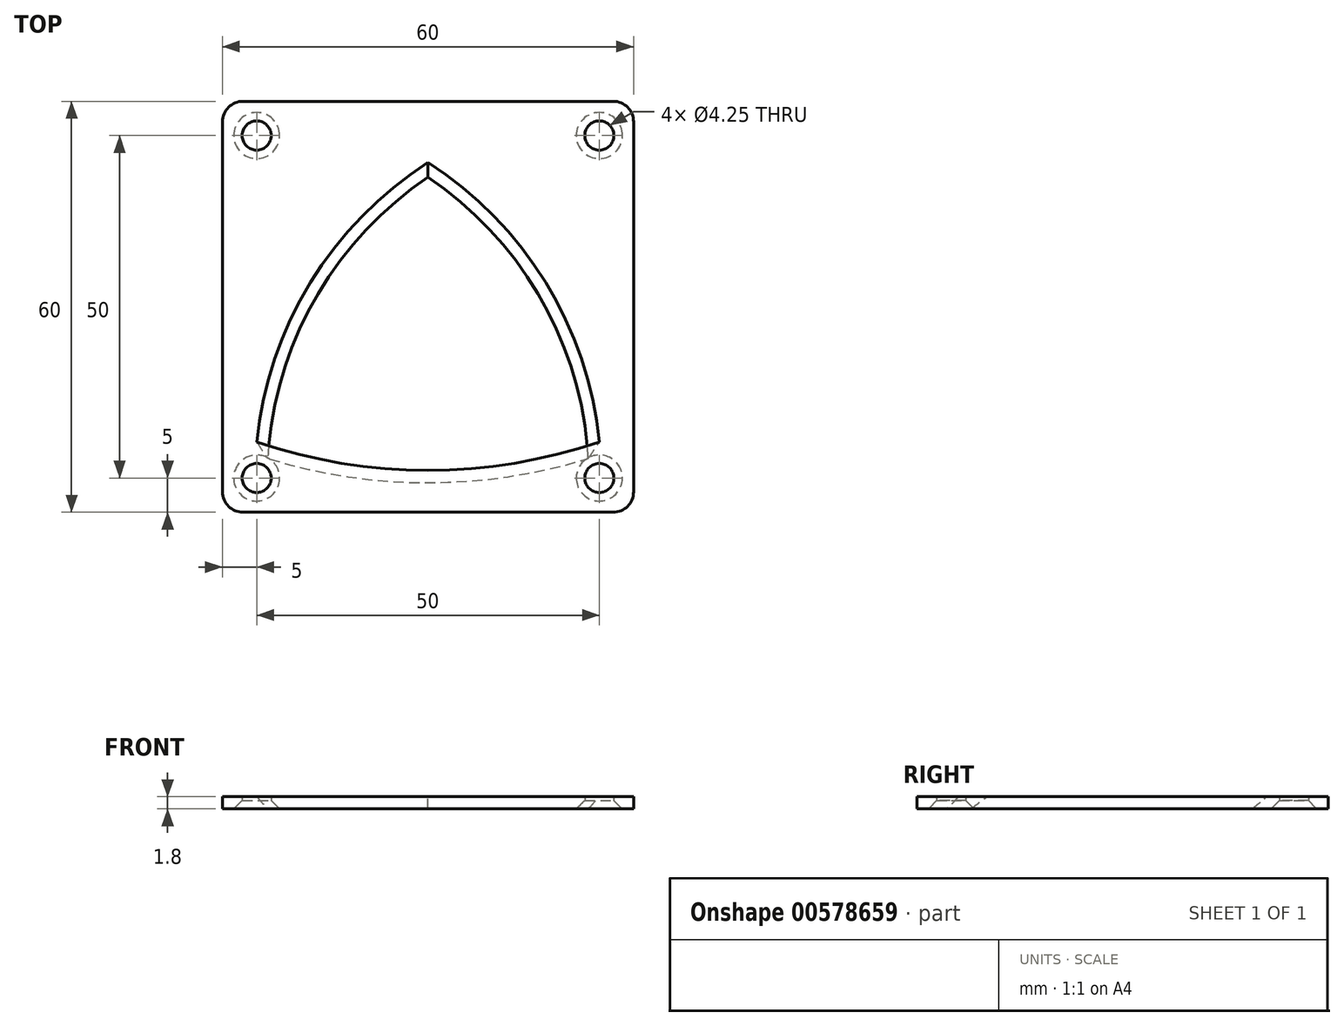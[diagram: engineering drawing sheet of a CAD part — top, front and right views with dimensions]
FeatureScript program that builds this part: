
annotation { "Feature Type Name" : "Feature", "Feature Type Description" : "" }
export const myFeature = defineFeature(function(context is Context, id is Id, definition is map)
    precondition{}
    {
        {
            var Q0;
            Q0=qCreatedBy(makeId("Top.planeOp"),FACE);
            var sketch = newSketch(context, id + "F0", { "sketchPlane" : qUnion([Q0])});
            skLineSegment(sketch, "E0.bottom", {"start": v(25, -25) * mm, "end": v(-25, -25) * mm});
            skLineSegment(sketch, "E0.top", {"start": v(25, 25) * mm, "end": v(-25, 25) * mm});
            skLineSegment(sketch, "E0.left", {"start": v(25, -25) * mm, "end": v(25, 25) * mm});
            skLineSegment(sketch, "E0.right", {"start": v(-25, -25) * mm, "end": v(-25, 25) * mm});
            skPoint(sketch, "E0.middle", {"position": v(0, 0) * mm});
            skLineSegment(sketch, "E1.bottom", {"start": v(30, -30) * mm, "end": v(-30, -30) * mm});
            skLineSegment(sketch, "E1.top", {"start": v(30, 30) * mm, "end": v(-30, 30) * mm});
            skLineSegment(sketch, "E1.left", {"start": v(30, -30) * mm, "end": v(30, 30) * mm});
            skLineSegment(sketch, "E1.right", {"start": v(-30, -30) * mm, "end": v(-30, 30) * mm});
            skLineSegment(sketch, "E2.bottom", {"start": v(-30, -30) * mm, "end": v(30, -30) * mm});
            skLineSegment(sketch, "E2.top", {"start": v(-30, -50) * mm, "end": v(30, -50) * mm});
            skLineSegment(sketch, "E2.left", {"start": v(-30, -30) * mm, "end": v(-30, -50) * mm});
            skLineSegment(sketch, "E2.right", {"start": v(30, -30) * mm, "end": v(30, -50) * mm});
            skPoint(sketch, "E3", {"position": v(-12.75, -33.65) * mm});
            skPoint(sketch, "E4", {"position": v(12.75, -33.65) * mm});
            skPoint(sketch, "E5", {"position": v(0, -33.65) * mm});
            skPoint(sketch, "E5.positionSnap0", {"position": v(0, -30) * mm});
            skLineSegment(sketch, "E6", {"start": v(-20, -20) * mm, "end": v(20, -20) * mm});
            skLineSegment(sketch, "E7", {"start": v(20, -20) * mm, "end": v(0, 15) * mm});
            skLineSegment(sketch, "E8", {"start": v(0, 15) * mm, "end": v(-20, -20) * mm});
            skPoint(sketch, "E9", {"position": v(0, -20) * mm});
            skArc(sketch, "E10", {"start": v(-20, -20) * mm, "mid": v(0, -22.68) * mm, "end": v(20, -20) * mm});
            skArc(sketch, "E11", {"start": v(0, 15) * mm, "mid": v(-13.68, -0.4) * mm, "end": v(-20, -20) * mm});
            skArc(sketch, "E12", {"start": v(20, -20) * mm, "mid": v(13.68, -0.4) * mm, "end": v(0, 15) * mm});
            skSolve(sketch);
        }
        {
            var Q0;
            Q0=makeQuery(id+"F0.imprint","IMPRINT",FACE,{"disambiguationData":[TD([[makeQuery(id+"F0.imprint","IMPRINT",EDGE,{"derivedFrom":sQuery(id+"F0.wireOp",EDGE,"E2.bottom")}),-1.0]])]});
            var Q1;
            Q1=makeQuery(id+"F0.imprint","IMPRINT",FACE,{"disambiguationData":[TD([[makeQuery(id+"F0.imprint","IMPRINT",EDGE,{"derivedFrom":sQuery(id+"F0.wireOp",EDGE,"E0.bottom")}),1.0]])]});
            var Q2;
            Q2=makeQuery(id+"F0.imprint","IMPRINT",FACE,{"disambiguationData":[TD([[makeQuery(id+"F0.imprint","IMPRINT",EDGE,{"derivedFrom":sQuery(id+"F0.wireOp",EDGE,"E0.bottom")}),-1.0]])]});
            extrude(context, id + "F1", {"entities" : qUnion([Q0, Q1, Q2]), "depth" : 1.8 * mm, "offsetDistance" : 25 * mm});
        }
        {
            var Q0;
            Q0=sQuery(id+"F0.wireOp",VERTEX,"E0.right.start");
            var Q1;
            Q1=sQuery(id+"F0.wireOp",VERTEX,"E0.left.start");
            var Q2;
            Q2=sQuery(id+"F0.wireOp",VERTEX,"E0.left.end");
            var Q3;
            Q3=sQuery(id+"F0.wireOp",VERTEX,"E0.right.end");
            var Q4;
            Q4=makeQuery(id+"F1.opExtrude","SWEPT_BODY",BODY,{"disambiguationData":[OSD([sQuery(id+"F0.wireOp",EDGE,"E1.top"),sQuery(id+"F0.wireOp",EDGE,"E1.left"),sQuery(id+"F0.wireOp",EDGE,"E1.right"),sQuery(id+"F0.wireOp",EDGE,"E2.top"),sQuery(id+"F0.wireOp",EDGE,"E2.left"),sQuery(id+"F0.wireOp",EDGE,"E2.right"),sQuery(id+"F0.wireOp",EDGE,"E10"),sQuery(id+"F0.wireOp",EDGE,"E11"),sQuery(id+"F0.wireOp",EDGE,"E12")])]});
            hole(context, id + "F2", {"style" : HoleStyle.C_SINK, "endStyle" : HoleEndStyle.BLIND, "oppositeDirection" : true, "holeDiameter" : 4.25 * mm, "cSinkDiameter" : 6.72 * mm, "cSinkAngle" : 90 * degree, "majorDiameter" : 5 * mm, "holeDepth" : 15 * mm, "isTappedThrough" : true, "tappedDepth" : 12 * mm, "tapClearance" : 3, "locations" : qUnion([Q0, Q1, Q2, Q3]), "scope" : qUnion([Q4])});
        }
        {
            var Q0;
            Q0=sQuery(id+"F0.wireOp",VERTEX,"E3");
            var Q1;
            Q1=sQuery(id+"F0.wireOp",VERTEX,"E4");
            var Q2;
            Q2=makeQuery(id+"F1.opExtrude","SWEPT_BODY",BODY,{"disambiguationData":[OSD([sQuery(id+"F0.wireOp",EDGE,"E1.top"),sQuery(id+"F0.wireOp",EDGE,"E1.left"),sQuery(id+"F0.wireOp",EDGE,"E1.right"),sQuery(id+"F0.wireOp",EDGE,"E2.top"),sQuery(id+"F0.wireOp",EDGE,"E2.left"),sQuery(id+"F0.wireOp",EDGE,"E2.right"),sQuery(id+"F0.wireOp",EDGE,"E10"),sQuery(id+"F0.wireOp",EDGE,"E11"),sQuery(id+"F0.wireOp",EDGE,"E12")])]});
            hole(context, id + "F3", {"style" : HoleStyle.C_BORE, "endStyle" : HoleEndStyle.BLIND, "oppositeDirection" : true, "holeDiameter" : 3 * mm, "cBoreDiameter" : 6.5 * mm, "cBoreDepth" : .4 * mm, "majorDiameter" : 5 * mm, "holeDepth" : 15 * mm, "isTappedThrough" : true, "tappedDepth" : 12 * mm, "tapClearance" : 3, "locations" : qUnion([Q0, Q1]), "scope" : qUnion([Q2])});
        }
        {
            var Q0;
            Q0=makeQuery(id+"F1.opExtrude","SWEPT_EDGE",EDGE,{"disambiguationData":[OSD([sQuery(id+"F0.wireOp",EDGE,"E1.top"),sQuery(id+"F0.wireOp",EDGE,"E1.left")])]});
            var Q1;
            Q1=makeQuery(id+"F1.opExtrude","SWEPT_EDGE",EDGE,{"disambiguationData":[OSD([sQuery(id+"F0.wireOp",EDGE,"E1.top"),sQuery(id+"F0.wireOp",EDGE,"E1.right")])]});
            var Q2;
            Q2=makeQuery(id+"F1.opExtrude","SWEPT_EDGE",EDGE,{"disambiguationData":[OSD([sQuery(id+"F0.wireOp",EDGE,"E2.top"),sQuery(id+"F0.wireOp",EDGE,"E2.left")])]});
            var Q3;
            Q3=makeQuery(id+"F1.opExtrude","SWEPT_EDGE",EDGE,{"disambiguationData":[OSD([sQuery(id+"F0.wireOp",EDGE,"E2.top"),sQuery(id+"F0.wireOp",EDGE,"E2.right")])]});
            fillet(context, id + "F4", {"entities" : qUnion([Q0, Q1, Q2, Q3]), "radius" : 3 * mm, "tangentPropagation" : true, "allowEdgeOverflow" : false});
        }
        {
            var Q0;
            Q0=makeQuery(id+"F1.opExtrude","CAP_EDGE",EDGE,{"disambiguationData":[OSD([sQuery(id+"F0.wireOp",EDGE,"E11")])],"isStart":false});
            var Q1;
            Q1=makeQuery(id+"F1.opExtrude","CAP_EDGE",EDGE,{"disambiguationData":[OSD([sQuery(id+"F0.wireOp",EDGE,"E12")])],"isStart":false});
            chamfer(context, id + "F5", {"entities" : qUnion([Q0, Q1]), "width" : 5 * mm, "tangentPropagation" : true});
        }
        {
            var Q0;
            Q0=makeQuery(id+"F1.opExtrude","CAP_EDGE",EDGE,{"disambiguationData":[OSD([sQuery(id+"F0.wireOp",EDGE,"E10")])],"isStart":true});
            chamfer(context, id + "F6", {"entities" : qUnion([Q0]), "width" : 3 * mm, "tangentPropagation" : true});
        }
    });
